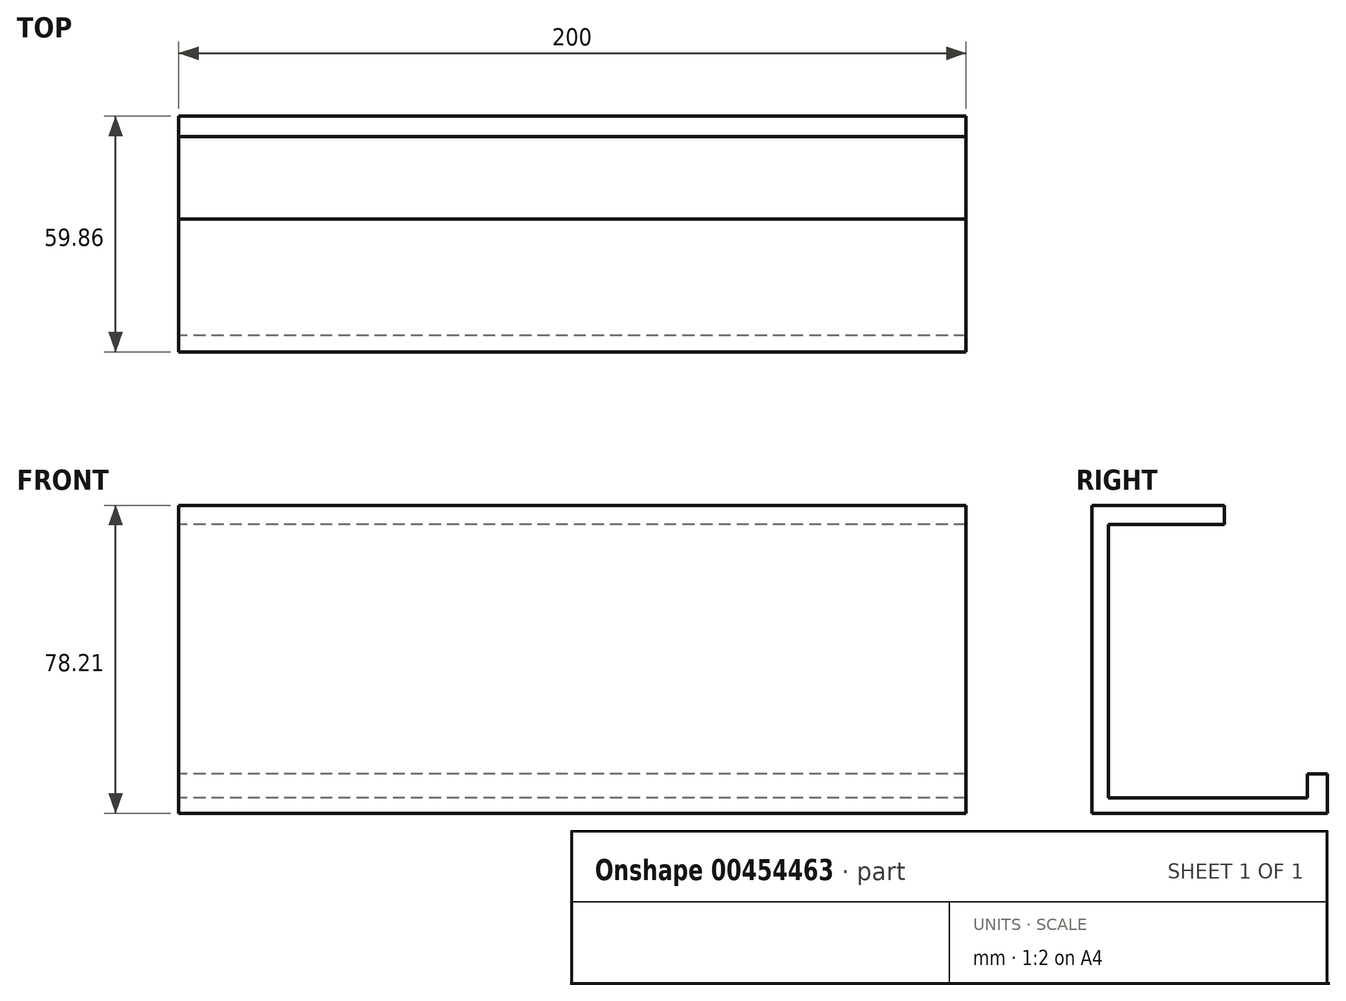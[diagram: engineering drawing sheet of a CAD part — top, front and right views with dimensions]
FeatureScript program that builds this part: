
annotation { "Feature Type Name" : "Feature", "Feature Type Description" : "" }
export const myFeature = defineFeature(function(context is Context, id is Id, definition is map)
    precondition{}
    {
        {
            var Q0;
            Q0=qCreatedBy(makeId("Right.planeOp"),FACE);
            var sketch = newSketch(context, id + "F0", { "sketchPlane" : qUnion([Q0])});
            skLineSegment(sketch, "E0", {"start": v(0, -30.08) * mm, "end": v(-59.86, -30.08) * mm});
            skLineSegment(sketch, "E1", {"start": v(-59.86, -30.08) * mm, "end": v(-59.86, 48.13) * mm});
            skLineSegment(sketch, "E2", {"start": v(-59.86, 48.13) * mm, "end": v(-26.17, 48.13) * mm});
            skLineSegment(sketch, "E3", {"start": v(-26.17, 48.13) * mm, "end": v(-26.17, 43.31) * mm});
            skLineSegment(sketch, "E4", {"start": v(-26.17, 43.31) * mm, "end": v(-55.65, 43.31) * mm});
            skLineSegment(sketch, "E5", {"start": v(-55.65, 43.31) * mm, "end": v(-55.65, -26.17) * mm});
            skLineSegment(sketch, "E6", {"start": v(-55.65, -26.17) * mm, "end": v(0, -26.17) * mm});
            skLineSegment(sketch, "E7", {"start": v(0, -26.17) * mm, "end": v(0, -30.08) * mm});
            skLineSegment(sketch, "E8", {"start": v(-5.11, -26.17) * mm, "end": v(-5.11, -20.15) * mm});
            skLineSegment(sketch, "E9", {"start": v(-5.11, -20.15) * mm, "end": v(0, -20.15) * mm});
            skLineSegment(sketch, "E10", {"start": v(0, -20.15) * mm, "end": v(0, -30.08) * mm});
            skSolve(sketch);
        }
        {
            var Q0;
            {var subQ3=sQuery(id+"F0.wireOp",EDGE,"E8");Q0=makeQuery(id+"F0.imprint","IMPRINT",FACE,{"disambiguationData":[TD([[makeQuery(id+"F0.imprint","IMPRINT",EDGE,{"derivedFrom":subQ3}),-1.0]])]});}
            var Q1;
            {var subQ0=sQuery(id+"F0.wireOp",EDGE,"E0");Q1=makeQuery(id+"F0.imprint","IMPRINT",FACE,{"disambiguationData":[TD([[makeQuery(id+"F0.imprint","IMPRINT",EDGE,{"derivedFrom":subQ0}),-1.0]])]});}
            extrude(context, id + "F1", {"entities" : qUnion([Q0, Q1]), "depth" : 200 * mm});
        }
    });
